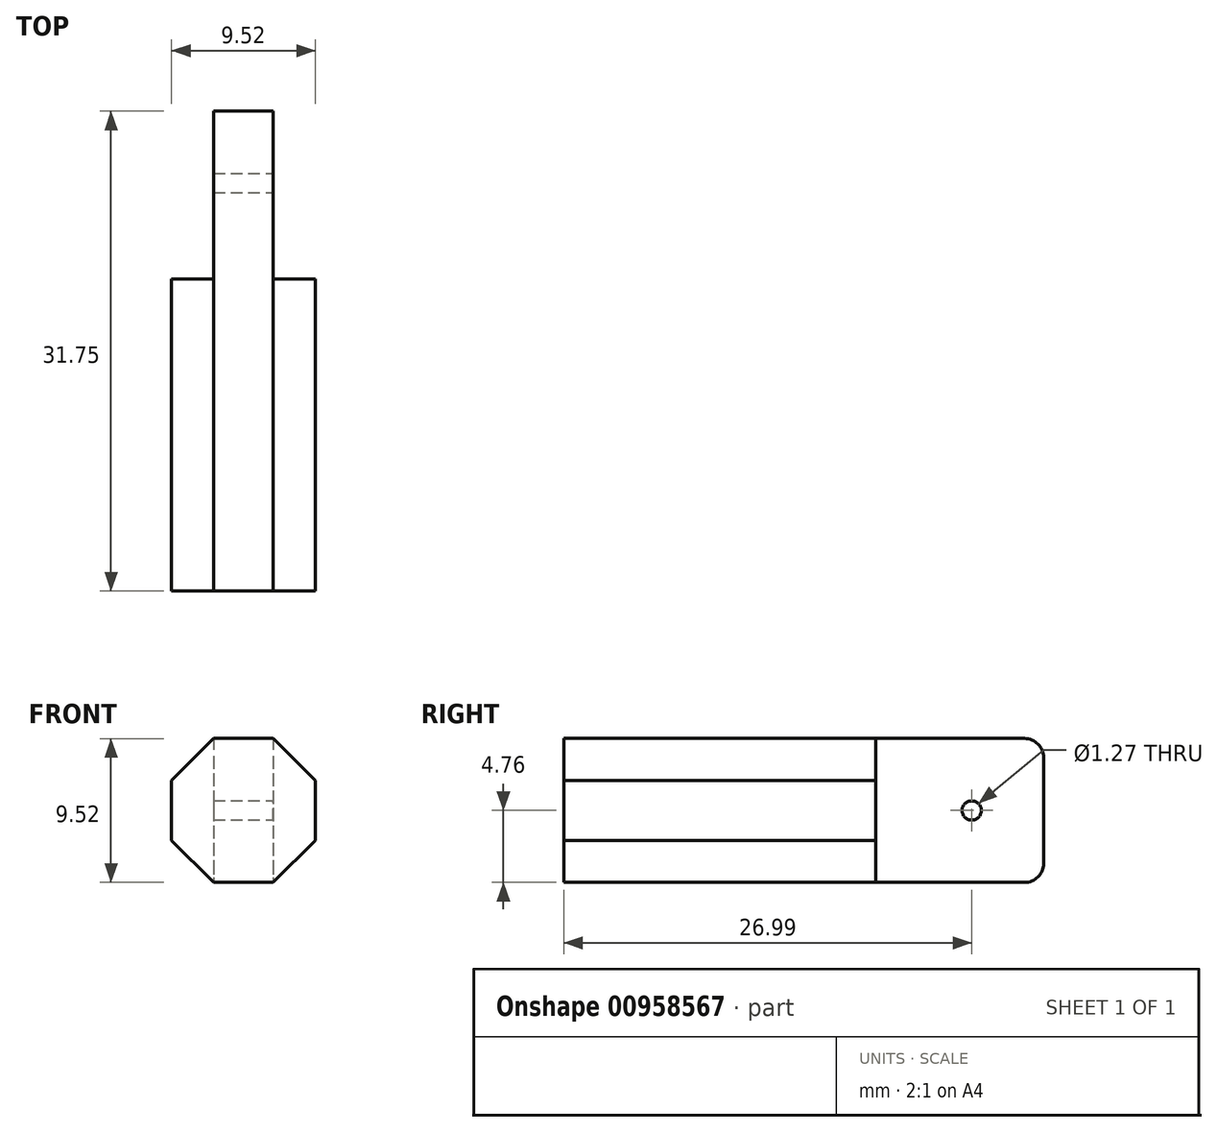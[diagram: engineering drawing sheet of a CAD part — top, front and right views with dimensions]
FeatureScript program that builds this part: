
annotation { "Feature Type Name" : "Feature", "Feature Type Description" : "" }
export const myFeature = defineFeature(function(context is Context, id is Id, definition is map)
    precondition{}
    {
        {
            var Q0;
            Q0=qCreatedBy(makeId("Front.planeOp"),FACE);
            var sketch = newSketch(context, id + "F0", { "sketchPlane" : qUnion([Q0])});
            skCircle(sketch, "E0.cCircle", {"center": v(0, 0) * mm, "radius": 4.76 * mm, "construction": true});
            skLineSegment(sketch, "E0.0", {"start": v(-1.97, 4.76) * mm, "end": v(1.97, 4.76) * mm});
            skLineSegment(sketch, "E0.1", {"start": v(1.97, 4.76) * mm, "end": v(4.76, 1.97) * mm});
            skLineSegment(sketch, "E0.2", {"start": v(4.76, 1.97) * mm, "end": v(4.76, -1.97) * mm});
            skLineSegment(sketch, "E0.3", {"start": v(4.76, -1.97) * mm, "end": v(1.97, -4.76) * mm});
            skLineSegment(sketch, "E0.4", {"start": v(1.97, -4.76) * mm, "end": v(-1.97, -4.76) * mm});
            skLineSegment(sketch, "E0.5", {"start": v(-1.97, -4.76) * mm, "end": v(-4.76, -1.97) * mm});
            skLineSegment(sketch, "E0.6", {"start": v(-4.76, -1.97) * mm, "end": v(-4.76, 1.97) * mm});
            skLineSegment(sketch, "E0.7", {"start": v(-4.76, 1.97) * mm, "end": v(-1.97, 4.76) * mm});
            skPoint(sketch, "E0.0.midPoint", {"position": v(0, 4.76) * mm});
            skSolve(sketch);
        }
        {
            var Q0;
            Q0=makeQuery(id+"F0.imprint","IMPRINT",FACE,{"disambiguationData":[TD([[makeQuery(id+"F0.imprint","IMPRINT",EDGE,{"derivedFrom":sQuery(id+"F0.wireOp",EDGE,"E0.0")}),-1.0]])]});
            extrude(context, id + "F1", {"entities" : qUnion([Q0]), "depth" : 20.64 * mm, "offsetDistance" : 25.4 * mm});
        }
        {
            var Q0;
            Q0=makeQuery(id+"F1.opExtrude","CAP_FACE",FACE,{"disambiguationData":[OSD([sQuery(id+"F0.wireOp",EDGE,"E0.0"),sQuery(id+"F0.wireOp",EDGE,"E0.1"),sQuery(id+"F0.wireOp",EDGE,"E0.2"),sQuery(id+"F0.wireOp",EDGE,"E0.3"),sQuery(id+"F0.wireOp",EDGE,"E0.4"),sQuery(id+"F0.wireOp",EDGE,"E0.5"),sQuery(id+"F0.wireOp",EDGE,"E0.6"),sQuery(id+"F0.wireOp",EDGE,"E0.7")])],"isStart":true});
            var sketch = newSketch(context, id + "F2", { "sketchPlane" : qUnion([Q0])});
            skLineSegment(sketch, "E1.bottom", {"start": v(-1.97, 4.76) * mm, "end": v(1.97, 4.76) * mm});
            skLineSegment(sketch, "E1.top", {"start": v(-1.97, -4.76) * mm, "end": v(1.97, -4.76) * mm});
            skLineSegment(sketch, "E1.left", {"start": v(-1.97, 4.76) * mm, "end": v(-1.97, -4.76) * mm});
            skLineSegment(sketch, "E1.right", {"start": v(1.97, 4.76) * mm, "end": v(1.97, -4.76) * mm});
            skSolve(sketch);
        }
        {
            var Q0;
            Q0=makeQuery(id+"F2.imprint","IMPRINT",FACE,{"disambiguationData":[TD([[makeQuery(id+"F2.imprint","IMPRINT",EDGE,{"derivedFrom":sQuery(id+"F2.wireOp",EDGE,"E1.bottom")}),1.0]])]});
            extrude(context, id + "F3", {"entities" : qUnion([Q0]), "operationType" : NewBodyOperationType.ADD, "depth" : 11.1 * mm, "offsetDistance" : 25.4 * mm});
        }
        {
            var Q0;
            Q0=makeQuery(id+"F3.opExtrude","CAP_EDGE",EDGE,{"disambiguationData":[OSD([sQuery(id+"F2.wireOp",EDGE,"E1.bottom")])],"isStart":false});
            var Q1;
            Q1=makeQuery(id+"F3.opExtrude","CAP_EDGE",EDGE,{"disambiguationData":[OSD([sQuery(id+"F2.wireOp",EDGE,"E1.top")])],"isStart":false});
            fillet(context, id + "F4", {"entities" : qUnion([Q0, Q1]), "radius" : 1.27 * mm, "tangentPropagation" : true, "allowEdgeOverflow" : false});
        }
        {
            var Q0;
            Q0=makeQuery(id+"F3.opExtrude","SWEPT_FACE",FACE,{"disambiguationData":[OSD([sQuery(id+"F2.wireOp",EDGE,"E1.left")])]});
            var sketch = newSketch(context, id + "F5", { "sketchPlane" : qUnion([Q0])});
            skPoint(sketch, "E2", {"position": v(6.35, 0) * mm});
            skSolve(sketch);
        }
        {
            var Q0;
            Q0=sQuery(id+"F5.wireOp",VERTEX,"E2");
            var Q1;
            Q1=makeQuery(id+"F1.opExtrude","SWEPT_BODY",BODY,{"disambiguationData":[OSD([sQuery(id+"F0.wireOp",EDGE,"E0.0"),sQuery(id+"F0.wireOp",EDGE,"E0.1"),sQuery(id+"F0.wireOp",EDGE,"E0.2"),sQuery(id+"F0.wireOp",EDGE,"E0.3"),sQuery(id+"F0.wireOp",EDGE,"E0.4"),sQuery(id+"F0.wireOp",EDGE,"E0.5"),sQuery(id+"F0.wireOp",EDGE,"E0.6"),sQuery(id+"F0.wireOp",EDGE,"E0.7")])]});
            hole(context, id + "F6", {"style" : HoleStyle.SIMPLE, "endStyle" : HoleEndStyle.BLIND, "holeDiameter" : 1.27 * mm, "majorDiameter" : 6.35 * mm, "holeDepth" : 25.4 * mm, "isTappedThrough" : true, "tappedDepth" : 12.7 * mm, "tapClearance" : 3, "startFromSketch" : true, "locations" : qUnion([Q0]), "scope" : qUnion([Q1])});
        }
    });
